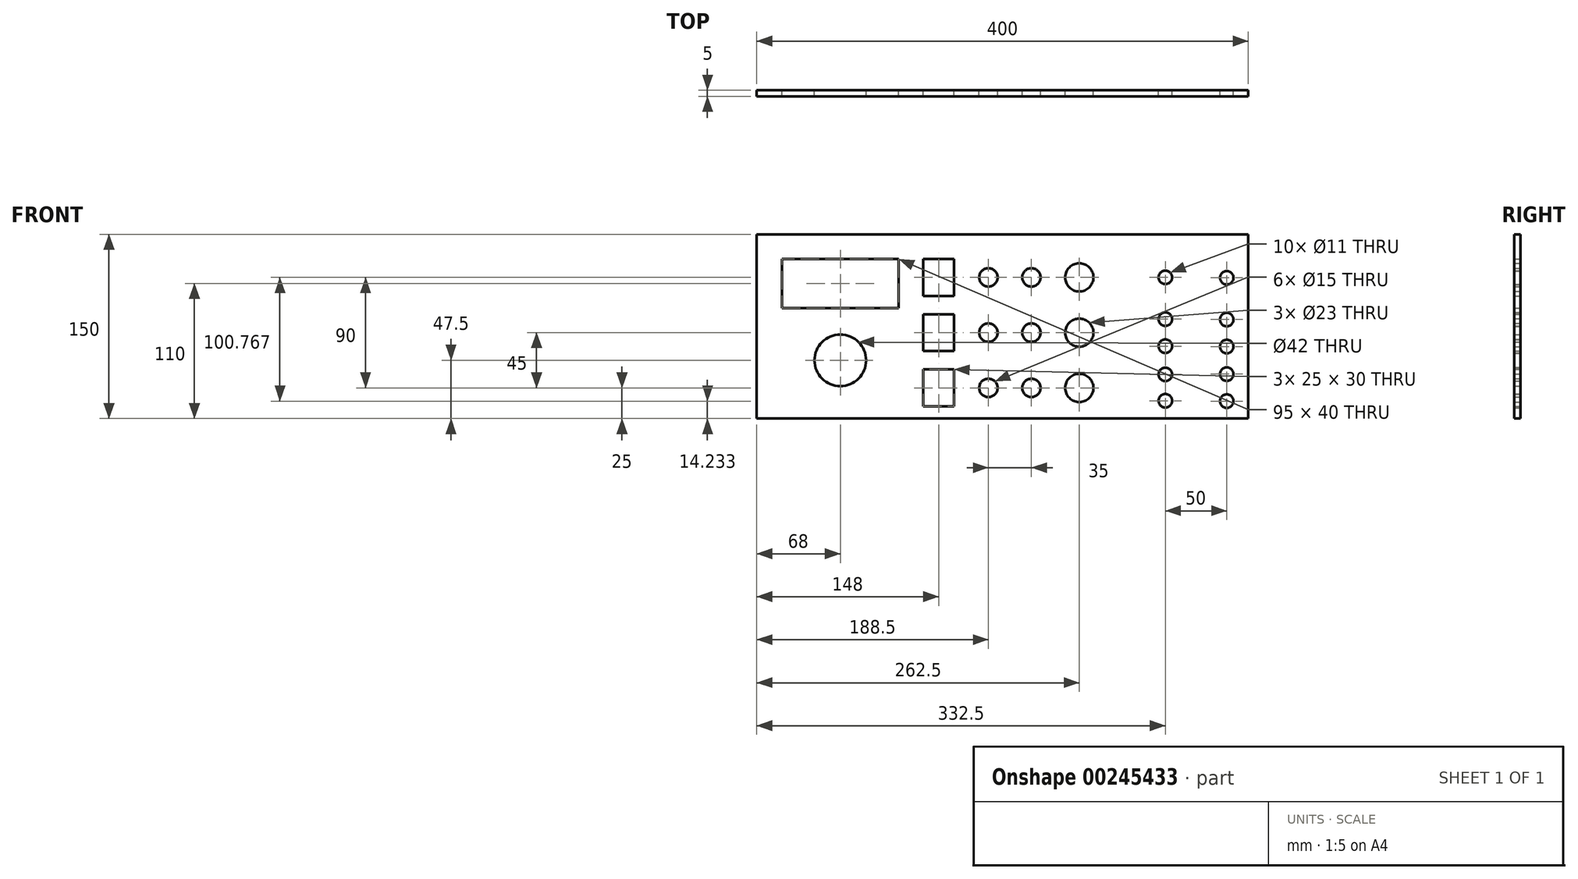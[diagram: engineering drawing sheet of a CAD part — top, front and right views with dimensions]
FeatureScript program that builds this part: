
annotation { "Feature Type Name" : "Feature", "Feature Type Description" : "" }
export const myFeature = defineFeature(function(context is Context, id is Id, definition is map)
    precondition{}
    {
        {
            var Q0;
            Q0=qCreatedBy(makeId("Front.planeOp"),FACE);
            var sketch = newSketch(context, id + "F0", { "sketchPlane" : qUnion([Q0])});
            skLineSegment(sketch, "E0", {"start": v(0, -65) * mm, "end": v(-12.5, -65) * mm});
            skLineSegment(sketch, "E1", {"start": v(-12.5, -65) * mm, "end": v(-12.5, -35) * mm});
            skLineSegment(sketch, "E2", {"start": v(-12.5, -35) * mm, "end": v(12.5, -35) * mm});
            skLineSegment(sketch, "E3", {"start": v(12.5, -35) * mm, "end": v(12.5, -65) * mm});
            skLineSegment(sketch, "E4", {"start": v(12.5, -65) * mm, "end": v(0, -65) * mm});
            skLineSegment(sketch, "E5", {"start": v(0, 55) * mm, "end": v(-12.5, 55) * mm});
            skLineSegment(sketch, "E6", {"start": v(-12.5, 55) * mm, "end": v(-12.5, 25) * mm});
            skLineSegment(sketch, "E7", {"start": v(-12.5, 25) * mm, "end": v(12.5, 25) * mm});
            skLineSegment(sketch, "E8", {"start": v(12.5, 25) * mm, "end": v(12.5, 55) * mm});
            skLineSegment(sketch, "E9", {"start": v(12.5, 55) * mm, "end": v(0, 55) * mm});
            skPoint(sketch, "E10.middle", {"position": v(0, -5) * mm});
            skLineSegment(sketch, "E11", {"start": v(0, 10) * mm, "end": v(12.5, 10) * mm});
            skLineSegment(sketch, "E12", {"start": v(12.5, 10) * mm, "end": v(12.5, -20) * mm});
            skLineSegment(sketch, "E13", {"start": v(12.5, -20) * mm, "end": v(-12.5, -20) * mm});
            skLineSegment(sketch, "E14", {"start": v(-12.5, -20) * mm, "end": v(-12.5, 10) * mm});
            skLineSegment(sketch, "E15", {"start": v(-12.5, 10) * mm, "end": v(0, 10) * mm});
            skCircle(sketch, "E16", {"center": v(40.5, -5) * mm, "radius": 7.5 * mm});
            skCircle(sketch, "E17", {"center": v(40.5, -50) * mm, "radius": 7.5 * mm});
            skCircle(sketch, "E18", {"center": v(40.5, 40) * mm, "radius": 7.5 * mm});
            skCircle(sketch, "E19", {"center": v(75.5, 40) * mm, "radius": 7.5 * mm});
            skCircle(sketch, "E20.MirrorC", {"center": v(75.5, -50) * mm, "radius": 7.5 * mm});
            skCircle(sketch, "E21", {"center": v(75.5, -5) * mm, "radius": 7.5 * mm});
            skCircle(sketch, "E22", {"center": v(114.5, 40) * mm, "radius": 11.5 * mm});
            skCircle(sketch, "E23", {"center": v(114.5, -5) * mm, "radius": 11.5 * mm});
            skCircle(sketch, "E24", {"center": v(114.5, -50) * mm, "radius": 11.5 * mm});
            skPoint(sketch, "E25.middle", {"position": v(-80, -5) * mm});
            skLineSegment(sketch, "E26.bottom", {"start": v(-127.5, 55) * mm, "end": v(-75, 55) * mm});
            skCircle(sketch, "E27", {"center": v(-80, -27.5) * mm, "radius": 21 * mm});
            skLineSegment(sketch, "E28", {"start": v(0, 75) * mm, "end": v(-148, 75) * mm});
            skLineSegment(sketch, "E29", {"start": v(0, 75) * mm, "end": v(252, 75) * mm});
            skLineSegment(sketch, "E30", {"start": v(0, -75) * mm, "end": v(252, -75) * mm});
            skLineSegment(sketch, "E31", {"start": v(252, -75) * mm, "end": v(252, 75) * mm});
            skLineSegment(sketch, "E32", {"start": v(0, -75) * mm, "end": v(-148, -75) * mm});
            skLineSegment(sketch, "E33", {"start": v(-148, -75) * mm, "end": v(-148, 75) * mm});
            skLineSegment(sketch, "E34", {"start": v(-32.5, 40) * mm, "end": v(-32.5, 55) * mm});
            skLineSegment(sketch, "E35", {"start": v(-32.5, 40) * mm, "end": v(-32.5, 15) * mm});
            skLineSegment(sketch, "E36", {"start": v(-32.5, 15) * mm, "end": v(-127.5, 15) * mm});
            skLineSegment(sketch, "E37", {"start": v(-127.5, 15) * mm, "end": v(-127.5, 55) * mm});
            skPoint(sketch, "E26.left.start.orphan", {"position": v(-180, 55) * mm});
            skCircle(sketch, "E38.MirrorC", {"center": v(184.5, -39) * mm, "radius": 5.5 * mm});
            skCircle(sketch, "E39.MirrorC", {"center": v(234.5, -38.77) * mm, "radius": 5.5 * mm});
            skCircle(sketch, "E40.MirrorC", {"center": v(184.5, -60.46) * mm, "radius": 5.5 * mm});
            skCircle(sketch, "E41.MirrorC", {"center": v(234.5, -60.77) * mm, "radius": 5.5 * mm});
            skCircle(sketch, "E42.MirrorC", {"center": v(184.5, -16) * mm, "radius": 5.5 * mm});
            skCircle(sketch, "E43.MirrorC", {"center": v(234.5, -16.3) * mm, "radius": 5.5 * mm});
            skCircle(sketch, "E44.MirrorC", {"center": v(234.5, 5.7) * mm, "radius": 5.5 * mm});
            skCircle(sketch, "E45.MirrorC", {"center": v(184.5, 6) * mm, "radius": 5.5 * mm});
            skCircle(sketch, "E46.MirrorC", {"center": v(184.5, 40) * mm, "radius": 5.5 * mm});
            skCircle(sketch, "E47.MirrorC", {"center": v(234.5, 39.7) * mm, "radius": 5.5 * mm});
            skLineSegment(sketch, "E48", {"start": v(-32.5, 55) * mm, "end": v(-75, 55) * mm});
            skSolve(sketch);
        }
        {
            var Q0;
            Q0=qSketchRegion(id+"F0",true);
            extrude(context, id + "F1", {"entities" : qUnion([Q0]), "depth" : 5 * mm});
        }
    });
